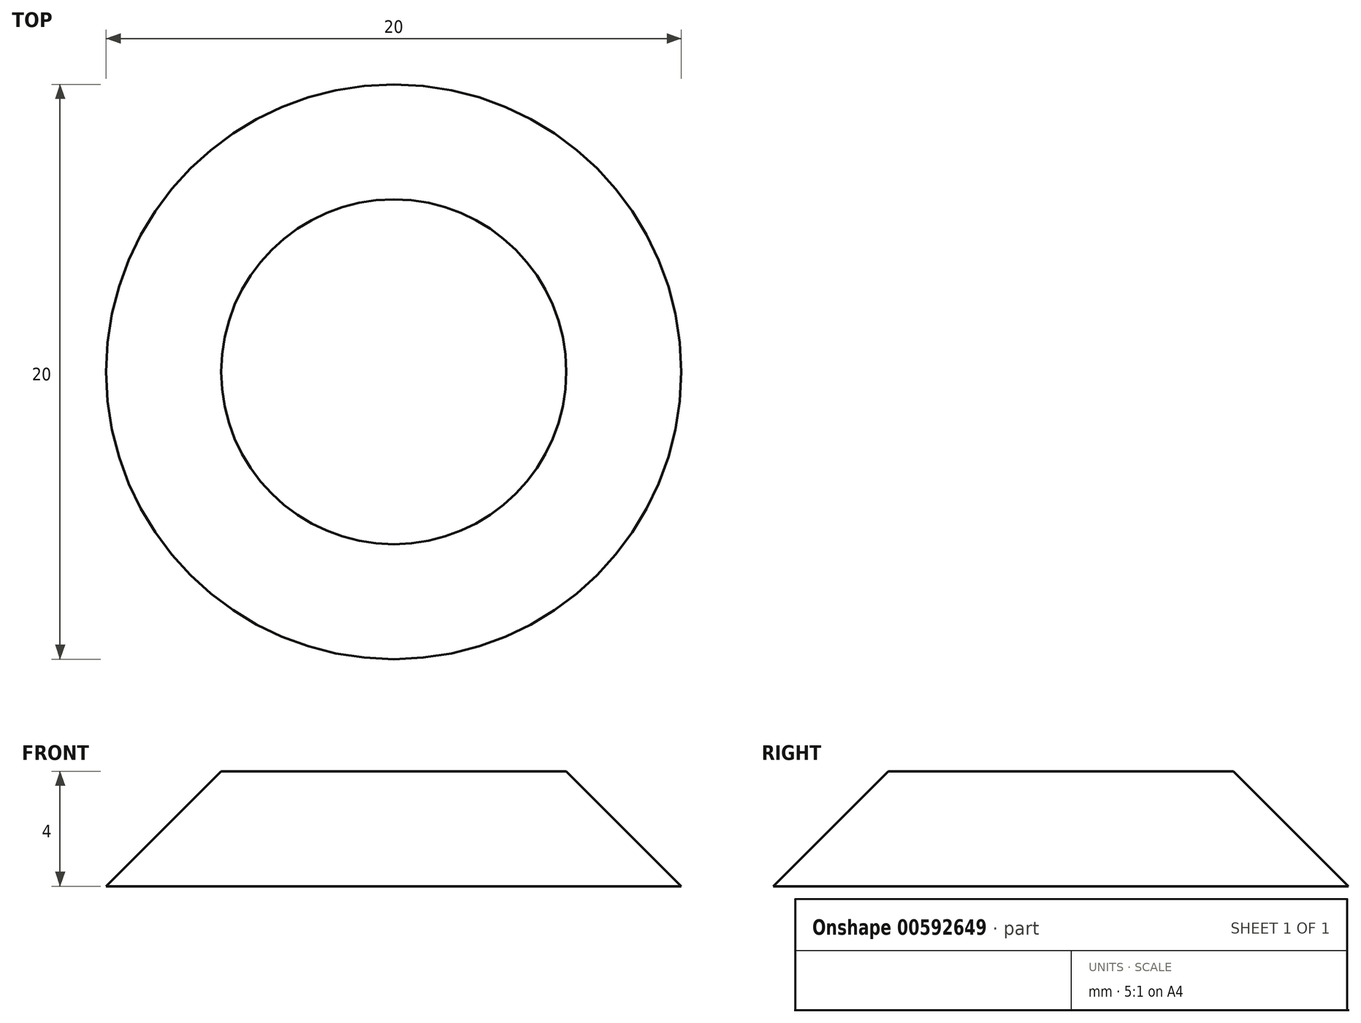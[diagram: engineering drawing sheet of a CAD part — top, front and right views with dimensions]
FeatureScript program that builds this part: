
annotation { "Feature Type Name" : "Feature", "Feature Type Description" : "" }
export const myFeature = defineFeature(function(context is Context, id is Id, definition is map)
    precondition{}
    {
        {
            var Q0;
            Q0=qCreatedBy(makeId("Front.planeOp"),FACE);
            var sketch = newSketch(context, id + "F0", { "sketchPlane" : qUnion([Q0])});
            skLineSegment(sketch, "E0", {"start": v(0, 0) * mm, "end": v(0, 4) * mm});
            skLineSegment(sketch, "E1", {"start": v(0, 4) * mm, "end": v(6, 4) * mm});
            skLineSegment(sketch, "E2", {"start": v(6, 4) * mm, "end": v(10, 0) * mm});
            skLineSegment(sketch, "E3", {"start": v(10, 0) * mm, "end": v(0, 0) * mm});
            skSolve(sketch);
        }
        {
            var Q0;
            Q0=makeQuery(id+"F0.imprint","IMPRINT",FACE,{"disambiguationData":[TD([[makeQuery(id+"F0.imprint","IMPRINT",EDGE,{"derivedFrom":sQuery(id+"F0.wireOp",EDGE,"E0")}),-1.0]])]});
            var Q1;
            Q1=sQuery(id+"F0.wireOp",EDGE,"E0");
            revolve(context, id + "F1", {"entities" : qUnion([Q0]), "axis" : qUnion([Q1]), "revolveType" : RevolveType.FULL});
        }
    });
